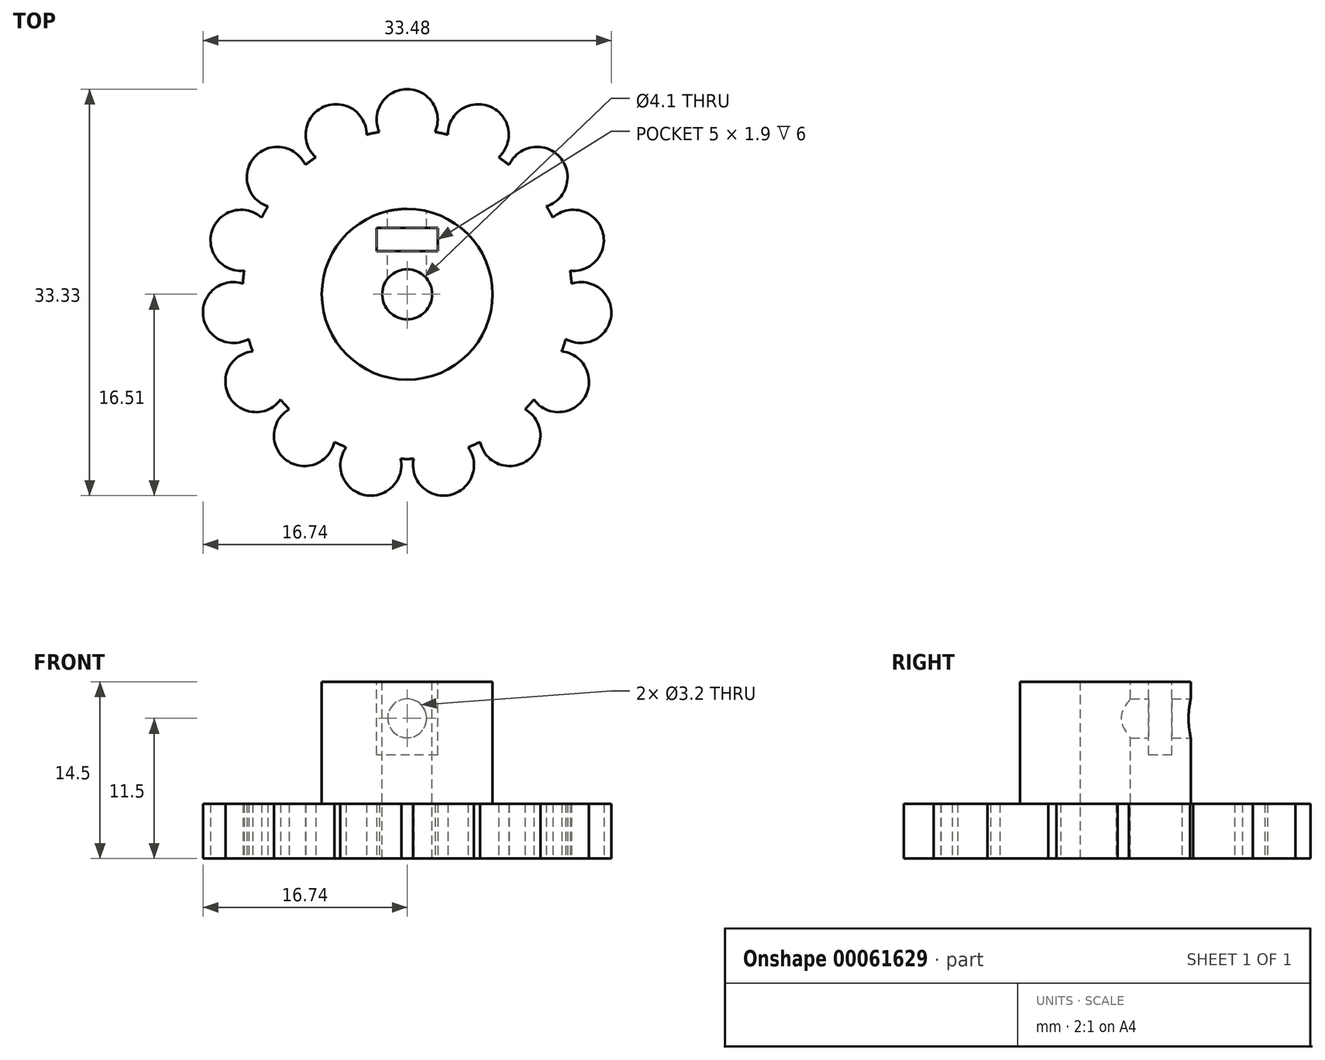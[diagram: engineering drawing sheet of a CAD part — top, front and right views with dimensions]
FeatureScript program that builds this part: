
annotation { "Feature Type Name" : "Feature", "Feature Type Description" : "" }
export const myFeature = defineFeature(function(context is Context, id is Id, definition is map)
    precondition{}
    {
        {
            var Q0;
            Q0=qCreatedBy(makeId("Top.planeOp"),FACE);
            var sketch = newSketch(context, id + "F0", { "sketchPlane" : qUnion([Q0])});
            skArc(sketch, "E0", {"start": v(2.28, 13.3) * mm, "mid": v(0, 16.82) * mm, "end": v(-2.28, 13.3) * mm});
            skArc(sketch, "E1.1.0", {"start": v(-3.32, 13.08) * mm, "mid": v(-6.84, 15.37) * mm, "end": v(-7.5, 11.23) * mm});
            skArc(sketch, "E1.2.0", {"start": v(-8.36, 10.6) * mm, "mid": v(-12.5, 11.25) * mm, "end": v(-11.42, 7.2) * mm});
            skArc(sketch, "E1.3.0", {"start": v(-11.95, 6.28) * mm, "mid": v(-16, 5.2) * mm, "end": v(-13.36, 1.94) * mm});
            skArc(sketch, "E1.4.0", {"start": v(-13.47, 0.88) * mm, "mid": v(-16.73, -1.76) * mm, "end": v(-13, -3.66) * mm});
            skArc(sketch, "E1.5.0", {"start": v(-12.67, -4.67) * mm, "mid": v(-14.57, -8.4) * mm, "end": v(-10.38, -8.63) * mm});
            skArc(sketch, "E1.6.0", {"start": v(-9.67, -9.42) * mm, "mid": v(-9.89, -13.6) * mm, "end": v(-5.97, -12.1) * mm});
            skArc(sketch, "E1.7.0", {"start": v(-5, -12.54) * mm, "mid": v(-3.5, -16.45) * mm, "end": v(-0.53, -13.49) * mm});
            skArc(sketch, "E1.8.0", {"start": v(0.53, -13.49) * mm, "mid": v(3.5, -16.45) * mm, "end": v(5, -12.54) * mm});
            skArc(sketch, "E1.9.0", {"start": v(5.97, -12.1) * mm, "mid": v(9.89, -13.6) * mm, "end": v(9.67, -9.42) * mm});
            skArc(sketch, "E1.10.0", {"start": v(10.38, -8.63) * mm, "mid": v(14.57, -8.41) * mm, "end": v(12.67, -4.67) * mm});
            skArc(sketch, "E1.11.0", {"start": v(13, -3.66) * mm, "mid": v(16.73, -1.76) * mm, "end": v(13.47, 0.88) * mm});
            skArc(sketch, "E1.12.0", {"start": v(13.36, 1.94) * mm, "mid": v(16, 5.2) * mm, "end": v(11.95, 6.28) * mm});
            skArc(sketch, "E1.13.0", {"start": v(11.42, 7.2) * mm, "mid": v(12.5, 11.25) * mm, "end": v(8.36, 10.6) * mm});
            skArc(sketch, "E1.14.0", {"start": v(7.5, 11.23) * mm, "mid": v(6.84, 15.37) * mm, "end": v(3.32, 13.08) * mm});
            skPoint(sketch, "E1.center", {"position": v(0, 0) * mm});
            skArc(sketch, "E2", {"start": v(-13.36, 1.94) * mm, "mid": v(-13.43, 1.41) * mm, "end": v(-13.47, 0.88) * mm});
            skArc(sketch, "E3.trimOffspring", {"start": v(-13, -3.66) * mm, "mid": v(-12.84, -4.17) * mm, "end": v(-12.67, -4.67) * mm});
            skArc(sketch, "E4.trimOffspring", {"start": v(-10.38, -8.63) * mm, "mid": v(-10.03, -9.03) * mm, "end": v(-9.67, -9.42) * mm});
            skArc(sketch, "E5.trimOffspring", {"start": v(-5.97, -12.1) * mm, "mid": v(-5.5, -12.33) * mm, "end": v(-5, -12.54) * mm});
            skArc(sketch, "E6.trimOffspring", {"start": v(-0.53, -13.49) * mm, "mid": v(0, -13.5) * mm, "end": v(0.53, -13.49) * mm});
            skArc(sketch, "E7.trimOffspring", {"start": v(5, -12.54) * mm, "mid": v(5.5, -12.33) * mm, "end": v(5.97, -12.1) * mm});
            skArc(sketch, "E8.trimOffspring", {"start": v(9.67, -9.42) * mm, "mid": v(10.03, -9.03) * mm, "end": v(10.38, -8.63) * mm});
            skArc(sketch, "E9.trimOffspring", {"start": v(12.67, -4.67) * mm, "mid": v(12.84, -4.17) * mm, "end": v(13, -3.66) * mm});
            skArc(sketch, "E10.trimOffspring", {"start": v(13.47, 0.88) * mm, "mid": v(13.43, 1.41) * mm, "end": v(13.36, 1.94) * mm});
            skArc(sketch, "E11.trimOffspring", {"start": v(11.95, 6.28) * mm, "mid": v(11.7, 6.75) * mm, "end": v(11.42, 7.2) * mm});
            skArc(sketch, "E12.trimOffspring", {"start": v(8.36, 10.6) * mm, "mid": v(7.94, 10.92) * mm, "end": v(7.5, 11.23) * mm});
            skArc(sketch, "E13.trimOffspring", {"start": v(3.32, 13.08) * mm, "mid": v(2.8, 13.2) * mm, "end": v(2.28, 13.3) * mm});
            skArc(sketch, "E14.trimOffspring", {"start": v(-2.28, 13.3) * mm, "mid": v(-2.8, 13.2) * mm, "end": v(-3.32, 13.08) * mm});
            skArc(sketch, "E15.trimOffspring", {"start": v(-7.5, 11.23) * mm, "mid": v(-7.94, 10.92) * mm, "end": v(-8.36, 10.6) * mm});
            skArc(sketch, "E16.trimOffspring", {"start": v(-11.42, 7.2) * mm, "mid": v(-11.7, 6.75) * mm, "end": v(-11.95, 6.28) * mm});
            skSolve(sketch);
        }
        {
            var Q0;
            Q0=makeQuery(id+"F0.imprint","IMPRINT",FACE,{"disambiguationData":[TD([[makeQuery(id+"F0.imprint","IMPRINT",EDGE,{"derivedFrom":sQuery(id+"F0.wireOp",EDGE,"E0")}),1.0]])]});
            extrude(context, id + "F1", {"entities" : qUnion([Q0]), "depth" : 4.5 * mm});
        }
        {
            var Q0;
            Q0=makeQuery(id+"F1.opExtrude","CAP_FACE",FACE,{"disambiguationData":[OSD([sQuery(id+"F0.wireOp",EDGE,"E0"),sQuery(id+"F0.wireOp",EDGE,"E1.1.0"),sQuery(id+"F0.wireOp",EDGE,"E1.2.0"),sQuery(id+"F0.wireOp",EDGE,"E1.3.0"),sQuery(id+"F0.wireOp",EDGE,"E1.4.0"),sQuery(id+"F0.wireOp",EDGE,"E1.5.0"),sQuery(id+"F0.wireOp",EDGE,"E1.6.0"),sQuery(id+"F0.wireOp",EDGE,"E1.7.0"),sQuery(id+"F0.wireOp",EDGE,"E1.8.0"),sQuery(id+"F0.wireOp",EDGE,"E1.9.0"),sQuery(id+"F0.wireOp",EDGE,"E1.10.0"),sQuery(id+"F0.wireOp",EDGE,"E1.11.0"),sQuery(id+"F0.wireOp",EDGE,"E1.12.0"),sQuery(id+"F0.wireOp",EDGE,"E1.13.0"),sQuery(id+"F0.wireOp",EDGE,"E1.14.0"),sQuery(id+"F0.wireOp",EDGE,"E2"),sQuery(id+"F0.wireOp",EDGE,"E3.trimOffspring"),sQuery(id+"F0.wireOp",EDGE,"E4.trimOffspring"),sQuery(id+"F0.wireOp",EDGE,"E5.trimOffspring"),sQuery(id+"F0.wireOp",EDGE,"E6.trimOffspring"),sQuery(id+"F0.wireOp",EDGE,"E7.trimOffspring"),sQuery(id+"F0.wireOp",EDGE,"E8.trimOffspring"),sQuery(id+"F0.wireOp",EDGE,"E9.trimOffspring"),sQuery(id+"F0.wireOp",EDGE,"E10.trimOffspring"),sQuery(id+"F0.wireOp",EDGE,"E11.trimOffspring"),sQuery(id+"F0.wireOp",EDGE,"E12.trimOffspring"),sQuery(id+"F0.wireOp",EDGE,"E13.trimOffspring"),sQuery(id+"F0.wireOp",EDGE,"E14.trimOffspring"),sQuery(id+"F0.wireOp",EDGE,"E15.trimOffspring"),sQuery(id+"F0.wireOp",EDGE,"E16.trimOffspring")])],"isStart":false});
            var sketch = newSketch(context, id + "F2", { "sketchPlane" : qUnion([Q0])});
            skCircle(sketch, "E17", {"center": v(0, 0) * mm, "radius": 7 * mm});
            skSolve(sketch);
        }
        {
            var Q0;
            Q0 = qSketchRegion(id + "F2", true);
            extrude(context, id + "F3", {"entities" : qUnion([Q0]), "operationType" : NewBodyOperationType.ADD, "depth" : 10 * mm});
        }
        {
            var Q0;
            Q0=makeQuery(id+"F3.opExtrude","CAP_FACE",FACE,{"disambiguationData":[OSD([sQuery(id+"F2.wireOp",EDGE,"E17")])],"isStart":false});
            var sketch = newSketch(context, id + "F4", { "sketchPlane" : qUnion([Q0])});
            skCircle(sketch, "E18", {"center": v(0, 0) * mm, "radius": 2.05 * mm});
            skSolve(sketch);
        }
        {
            var Q0;
            Q0=makeQuery(id+"F4.imprint","IMPRINT",FACE,{"disambiguationData":[TD([[makeQuery(id+"F4.imprint","IMPRINT",EDGE,{"derivedFrom":sQuery(id+"F4.wireOp",EDGE,"E18")}),1.0]])]});
            extrude(context, id + "F5", {"entities" : qUnion([Q0]), "operationType" : NewBodyOperationType.REMOVE, "oppositeDirection" : true, "depth" : 25 * mm});
        }
        {
            var Q0;
            Q0=makeQuery(id+"F3.opExtrude","CAP_FACE",FACE,{"disambiguationData":[OSD([sQuery(id+"F2.wireOp",EDGE,"E17")])],"isStart":false});
            var sketch = newSketch(context, id + "F6", { "sketchPlane" : qUnion([Q0])});
            skLineSegment(sketch, "E19.bottom", {"start": v(2.5, 5.45) * mm, "end": v(-2.5, 5.45) * mm});
            skLineSegment(sketch, "E19.top", {"start": v(2.5, 3.55) * mm, "end": v(-2.5, 3.55) * mm});
            skLineSegment(sketch, "E19.left", {"start": v(2.5, 5.45) * mm, "end": v(2.5, 3.55) * mm});
            skLineSegment(sketch, "E19.right", {"start": v(-2.5, 5.45) * mm, "end": v(-2.5, 3.55) * mm});
            skSolve(sketch);
        }
        {
            var Q0;
            Q0=makeQuery(id+"F6.imprint","IMPRINT",FACE,{"disambiguationData":[TD([[makeQuery(id+"F6.imprint","IMPRINT",EDGE,{"derivedFrom":sQuery(id+"F6.wireOp",EDGE,"E19.bottom")}),1.0]])]});
            extrude(context, id + "F7", {"entities" : qUnion([Q0]), "operationType" : NewBodyOperationType.REMOVE, "oppositeDirection" : true, "depth" : 6 * mm});
        }
        {
            var Q0;
            Q0=makeQuery(id+"F7.boolean.opBoolean","COPY",FACE,{"derivedFrom":makeQuery(id+"F7.opExtrude","SWEPT_FACE",FACE,{"disambiguationData":[OSD([sQuery(id+"F6.wireOp",EDGE,"E19.top")])]})});
            var sketch = newSketch(context, id + "F8", { "sketchPlane" : qUnion([Q0])});
            skCircle(sketch, "E20", {"center": v(0, 11.5) * mm, "radius": 1.6 * mm});
            skSolve(sketch);
        }
        {
            var Q0;
            Q0=makeQuery(id+"F8.imprint","IMPRINT",FACE,{"disambiguationData":[TD([[makeQuery(id+"F8.imprint","IMPRINT",EDGE,{"derivedFrom":sQuery(id+"F8.wireOp",EDGE,"E20")}),1.0]])]});
            extrude(context, id + "F9", {"entities" : qUnion([Q0]), "operationType" : NewBodyOperationType.REMOVE, "endBound" : BoundingType.UP_TO_NEXT, "oppositeDirection" : true, "depth" : 25 * mm, "hasSecondDirection" : true, "secondDirectionOppositeDirection" : false, "secondDirectionDepth" : 25 * mm});
        }
    });
